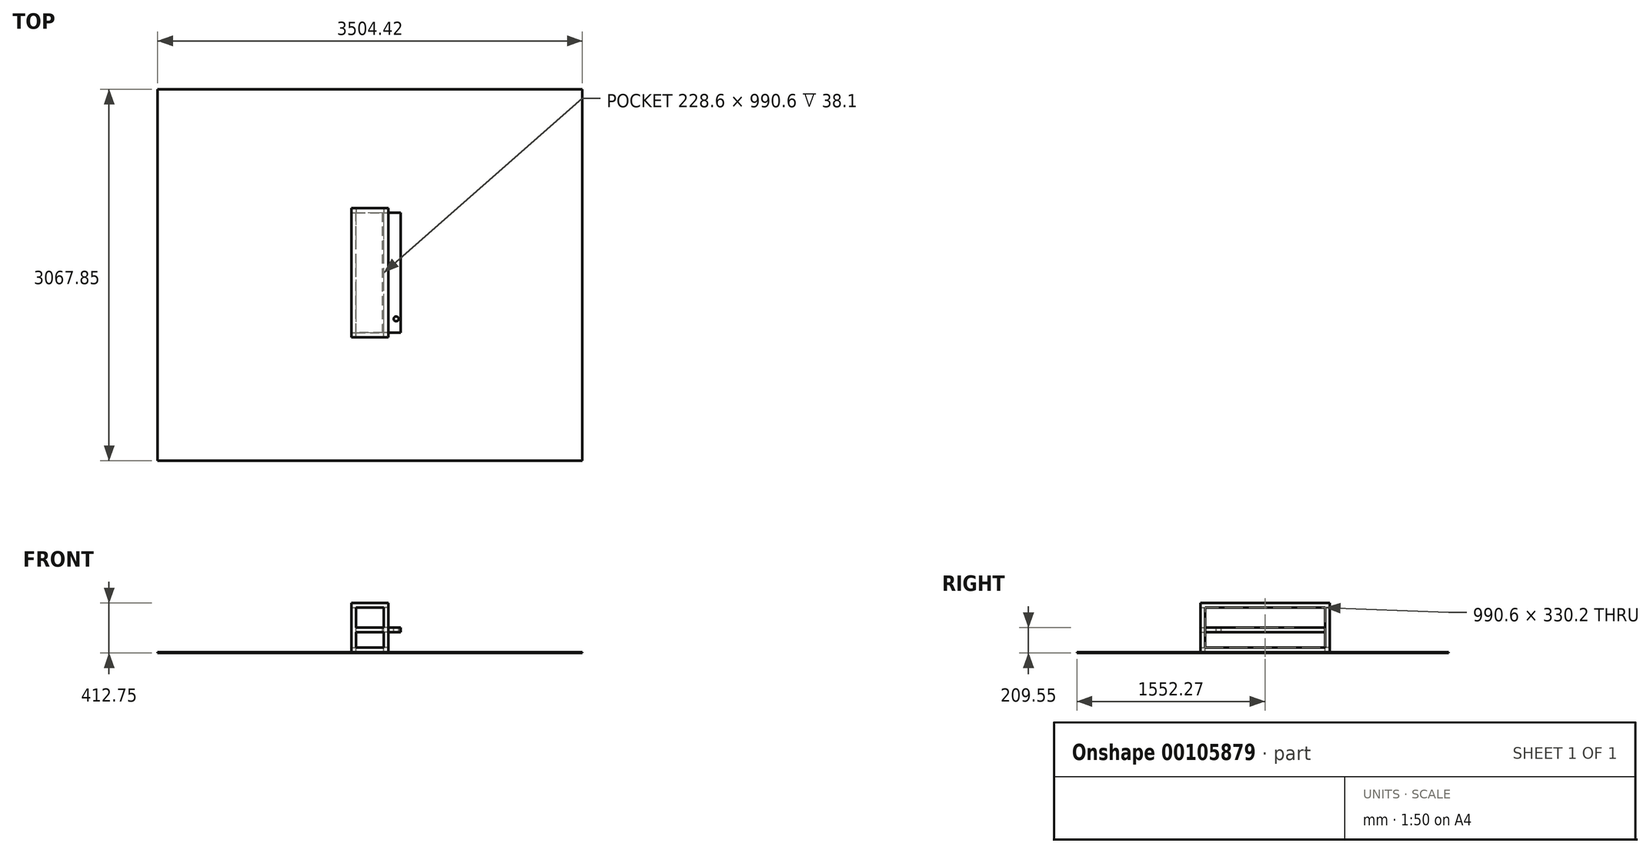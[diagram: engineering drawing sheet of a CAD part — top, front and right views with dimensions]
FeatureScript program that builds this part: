
annotation { "Feature Type Name" : "Feature", "Feature Type Description" : "" }
export const myFeature = defineFeature(function(context is Context, id is Id, definition is map)
    precondition{}
    {
        {
            var Q0;
            Q0=qCreatedBy(makeId("Top.planeOp"),FACE);
            var sketch = newSketch(context, id + "F0", { "sketchPlane" : qUnion([Q0])});
            skLineSegment(sketch, "E0.bottom", {"start": v(-152.4, 0) * mm, "end": v(152.4, 0) * mm});
            skLineSegment(sketch, "E0.top", {"start": v(-152.4, 1066.8) * mm, "end": v(152.4, 1066.8) * mm});
            skLineSegment(sketch, "E0.left", {"start": v(-152.4, 0) * mm, "end": v(-152.4, 1066.8) * mm});
            skLineSegment(sketch, "E0.right", {"start": v(152.4, 0) * mm, "end": v(152.4, 1066.8) * mm});
            skLineSegment(sketch, "E1", {"start": v(-152.4, 533.4) * mm, "end": v(152.4, 533.4) * mm, "construction": true});
            skSolve(sketch);
        }
        {
            var Q0;
            Q0 = qSketchRegion(id + "F0", true);
            extrude(context, id + "F1", {"entities" : qUnion([Q0]), "oppositeDirection" : true, "depth" : 38.1 * mm});
        }
        {
            var Q0;
            Q0=makeQuery(id+"F1.opExtrude","CAP_FACE",FACE,{"disambiguationData":[OSD([sQuery(id+"F0.wireOp",EDGE,"E0.bottom"),sQuery(id+"F0.wireOp",EDGE,"E0.top"),sQuery(id+"F0.wireOp",EDGE,"E0.left"),sQuery(id+"F0.wireOp",EDGE,"E0.right")])],"isStart":false});
            var sketch = newSketch(context, id + "F2", { "sketchPlane" : qUnion([Q0])});
            skLineSegment(sketch, "E2.bottom", {"start": v(-152.4, 0) * mm, "end": v(-114.3, 0) * mm});
            skLineSegment(sketch, "E2.top", {"start": v(-152.4, -38.1) * mm, "end": v(-114.3, -38.1) * mm});
            skLineSegment(sketch, "E2.left", {"start": v(-152.4, 0) * mm, "end": v(-152.4, -38.1) * mm});
            skLineSegment(sketch, "E2.right", {"start": v(-114.3, 0) * mm, "end": v(-114.3, -38.1) * mm});
            skLineSegment(sketch, "E3", {"start": v(0, 0) * mm, "end": v(0, -1066.8) * mm, "construction": true});
            skLineSegment(sketch, "E4", {"start": v(-152.4, -533.4) * mm, "end": v(152.4, -533.4) * mm, "construction": true});
            skLineSegment(sketch, "E5.MirrorCS", {"start": v(152.4, -38.1) * mm, "end": v(114.3, -38.1) * mm});
            skLineSegment(sketch, "E6.MirrorCS", {"start": v(152.4, 0) * mm, "end": v(152.4, -38.1) * mm});
            skLineSegment(sketch, "E7.MirrorCS", {"start": v(152.4, 0) * mm, "end": v(114.3, 0) * mm});
            skLineSegment(sketch, "E8.MirrorCS", {"start": v(114.3, 0) * mm, "end": v(114.3, -38.1) * mm});
            skLineSegment(sketch, "E9.MirrorCS", {"start": v(152.4, -1028.7) * mm, "end": v(114.3, -1028.7) * mm});
            skLineSegment(sketch, "E10.MirrorCS", {"start": v(-152.4, -1028.7) * mm, "end": v(-114.3, -1028.7) * mm});
            skLineSegment(sketch, "E11.MirrorCS", {"start": v(-114.3, -1066.8) * mm, "end": v(-114.3, -1028.7) * mm});
            skLineSegment(sketch, "E12.MirrorCS", {"start": v(114.3, -1066.8) * mm, "end": v(114.3, -1028.7) * mm});
            skLineSegment(sketch, "E13.MirrorCS", {"start": v(-152.4, -1066.8) * mm, "end": v(-114.3, -1066.8) * mm});
            skLineSegment(sketch, "E14.MirrorCS", {"start": v(152.4, -1066.8) * mm, "end": v(114.3, -1066.8) * mm});
            skLineSegment(sketch, "E15.MirrorCS", {"start": v(152.4, -1066.8) * mm, "end": v(152.4, -1028.7) * mm});
            skLineSegment(sketch, "E16.MirrorCS", {"start": v(-152.4, -1066.8) * mm, "end": v(-152.4, -1028.7) * mm});
            skSolve(sketch);
        }
        {
            var Q0;
            Q0 = qSketchRegion(id + "F2", true);
            extrude(context, id + "F3", {"entities" : qUnion([Q0]), "operationType" : NewBodyOperationType.ADD, "depth" : 330.2 * mm});
        }
        {
            var Q0;
            Q0=makeQuery(id+"F3.opExtrude","CAP_FACE",FACE,{"disambiguationData":[OSD([sQuery(id+"F2.wireOp",EDGE,"E2.bottom"),sQuery(id+"F2.wireOp",EDGE,"E2.top"),sQuery(id+"F2.wireOp",EDGE,"E2.left"),sQuery(id+"F2.wireOp",EDGE,"E2.right")])],"isStart":false});
            var sketch = newSketch(context, id + "F4", { "sketchPlane" : qUnion([Q0])});
            skLineSegment(sketch, "E17.bottom", {"start": v(-152.4, 0) * mm, "end": v(152.4, 0) * mm});
            skLineSegment(sketch, "E17.top", {"start": v(-152.4, -1066.8) * mm, "end": v(152.4, -1066.8) * mm});
            skLineSegment(sketch, "E17.left", {"start": v(-152.4, 0) * mm, "end": v(-152.4, -1066.8) * mm});
            skLineSegment(sketch, "E17.right", {"start": v(152.4, 0) * mm, "end": v(152.4, -1066.8) * mm});
            skLineSegment(sketch, "E18.bottom", {"start": v(-114.3, -38.1) * mm, "end": v(114.3, -38.1) * mm});
            skLineSegment(sketch, "E18.top", {"start": v(-114.3, -1028.7) * mm, "end": v(114.3, -1028.7) * mm});
            skLineSegment(sketch, "E18.left", {"start": v(-114.3, -38.1) * mm, "end": v(-114.3, -1028.7) * mm});
            skLineSegment(sketch, "E18.right", {"start": v(114.3, -38.1) * mm, "end": v(114.3, -1028.7) * mm});
            skSolve(sketch);
        }
        {
            var Q0;
            Q0 = qSketchRegion(id + "F4", true);
            extrude(context, id + "F5", {"entities" : qUnion([Q0]), "operationType" : NewBodyOperationType.ADD, "depth" : 38.1 * mm});
        }
        {
            var Q0;
            Q0=makeQuery(id+"F5.boolean.opBoolean","MERGE",FACE,{"derivedFrom":[makeQuery(id+"F3.boolean.opBoolean","MERGE",FACE,{"derivedFrom":[makeQuery(id+"F1.opExtrude","SWEPT_FACE",FACE,{"disambiguationData":[OSD([sQuery(id+"F0.wireOp",EDGE,"E0.bottom")])]}),makeQuery(id+"F3.opExtrude","SWEPT_FACE",FACE,{"disambiguationData":[OSD([sQuery(id+"F2.wireOp",EDGE,"E2.bottom")])]}),makeQuery(id+"F3.opExtrude","SWEPT_FACE",FACE,{"disambiguationData":[OSD([sQuery(id+"F2.wireOp",EDGE,"E7.MirrorCS")])]})]}),makeQuery(id+"F5.opExtrude","SWEPT_FACE",FACE,{"disambiguationData":[OSD([sQuery(id+"F4.wireOp",EDGE,"E17.bottom")])]})]});
            var sketch = newSketch(context, id + "F6", { "sketchPlane" : qUnion([Q0])});
            skCircle(sketch, "E19", {"center": v(152.4, 0) * mm, "radius": 812.8 * mm});
            skLineSegment(sketch, "E20", {"start": v(0, 0) * mm, "end": v(0, 812.8) * mm, "construction": true});
            skCircle(sketch, "E21", {"center": v(783.38, -203.2) * mm, "radius": 812.8 * mm});
            skPoint(sketch, "E22", {"position": v(114.3, -203.2) * mm});
            skSolve(sketch);
        }
        {
            var Q0;
            Q0=makeQuery(id+"F3.opExtrude","SWEPT_FACE",FACE,{"disambiguationData":[OSD([sQuery(id+"F2.wireOp",EDGE,"E2.right")])]});
            var sketch = newSketch(context, id + "F7", { "sketchPlane" : qUnion([Q0])});
            skLineSegment(sketch, "E23.bottom", {"start": v(0, -203.2) * mm, "end": v(38.1, -203.2) * mm});
            skLineSegment(sketch, "E23.top", {"start": v(0, -241.3) * mm, "end": v(38.1, -241.3) * mm});
            skLineSegment(sketch, "E23.left", {"start": v(0, -203.2) * mm, "end": v(0, -241.3) * mm});
            skLineSegment(sketch, "E23.right", {"start": v(38.1, -203.2) * mm, "end": v(38.1, -241.3) * mm});
            skSolve(sketch);
        }
        {
            var Q0;
            Q0 = qSketchRegion(id + "F7", true);
            var Q1;
            Q1=makeQuery(id+"F3.opExtrude","SWEPT_FACE",FACE,{"disambiguationData":[OSD([sQuery(id+"F2.wireOp",EDGE,"E8.MirrorCS")])]});
            extrude(context, id + "F8", {"entities" : qUnion([Q0]), "operationType" : NewBodyOperationType.ADD, "endBound" : BoundingType.UP_TO_SURFACE, "endBoundEntityFace" : qUnion([Q1]), "depth" : 25.4 * mm});
        }
        {
            var Q0;
            Q0=makeQuery(id+"F8.boolean.opBoolean","MERGE",FACE,{"derivedFrom":[makeQuery(id+"F3.opExtrude","SWEPT_FACE",FACE,{"disambiguationData":[OSD([sQuery(id+"F2.wireOp",EDGE,"E2.top")])]}),makeQuery(id+"F3.opExtrude","SWEPT_FACE",FACE,{"disambiguationData":[OSD([sQuery(id+"F2.wireOp",EDGE,"E5.MirrorCS")])]}),makeQuery(id+"F8.opExtrude","SWEPT_FACE",FACE,{"disambiguationData":[OSD([sQuery(id+"F7.wireOp",EDGE,"E23.right")])]})]});
            var sketch = newSketch(context, id + "F9", { "sketchPlane" : qUnion([Q0])});
            skLineSegment(sketch, "E24.bottom", {"start": v(-254, -203.2) * mm, "end": v(-101.6, -203.2) * mm});
            skLineSegment(sketch, "E24.top", {"start": v(-254, -241.3) * mm, "end": v(-101.6, -241.3) * mm});
            skLineSegment(sketch, "E24.left", {"start": v(-254, -203.2) * mm, "end": v(-254, -241.3) * mm});
            skLineSegment(sketch, "E24.right", {"start": v(-101.6, -203.2) * mm, "end": v(-101.6, -241.3) * mm});
            skSolve(sketch);
        }
        {
            var Q0;
            Q0 = qSketchRegion(id + "F9", true);
            var Q1;
            Q1=makeQuery(id+"F3.opExtrude","SWEPT_FACE",FACE,{"disambiguationData":[OSD([sQuery(id+"F2.wireOp",EDGE,"E10.MirrorCS")])]});
            extrude(context, id + "F10", {"entities" : qUnion([Q0]), "operationType" : NewBodyOperationType.ADD, "endBound" : BoundingType.UP_TO_SURFACE, "endBoundEntityFace" : qUnion([Q1]), "depth" : 25.4 * mm});
        }
        {
            var Q0;
            Q0 = qSketchRegion(id + "F9", true);
            var Q1;
            Q1=makeQuery(id+"F3.opExtrude","SWEPT_FACE",FACE,{"disambiguationData":[OSD([sQuery(id+"F2.wireOp",EDGE,"E10.MirrorCS")])]});
            extrude(context, id + "F11", {"entities" : qUnion([Q0]), "operationType" : NewBodyOperationType.ADD, "endBound" : BoundingType.UP_TO_SURFACE, "endBoundEntityFace" : qUnion([Q1]), "depth" : 25.4 * mm});
        }
        {
            var Q0;
            Q0=makeQuery(id+"F10.boolean.opBoolean","MERGE",FACE,{"derivedFrom":[makeQuery(id+"F8.opExtrude","SWEPT_FACE",FACE,{"disambiguationData":[OSD([sQuery(id+"F7.wireOp",EDGE,"E23.bottom")])]}),makeQuery(id+"F10.opExtrude","SWEPT_FACE",FACE,{"disambiguationData":[OSD([sQuery(id+"F9.wireOp",EDGE,"QMmYdaav-W8pb-V5HU-5jat-0M2pRndT3nIR.bottom")])]})]});
            var sketch = newSketch(context, id + "F12", { "sketchPlane" : qUnion([Q0])});
            skCircle(sketch, "E25", {"center": v(215.9, 152.4) * mm, "radius": 20.42 * mm});
            skSolve(sketch);
        }
        {
            var Q0;
            Q0 = qSketchRegion(id + "F12", true);
            extrude(context, id + "F13", {"entities" : qUnion([Q0]), "operationType" : NewBodyOperationType.REMOVE, "endBound" : BoundingType.UP_TO_NEXT, "oppositeDirection" : true, "depth" : 25.4 * mm});
        }
        {
            var Q0;
            Q0=makeQuery(id+"F5.opExtrude","CAP_FACE",FACE,{"disambiguationData":[OSD([sQuery(id+"F4.wireOp",EDGE,"E17.bottom"),sQuery(id+"F4.wireOp",EDGE,"E17.top"),sQuery(id+"F4.wireOp",EDGE,"E17.left"),sQuery(id+"F4.wireOp",EDGE,"E17.right"),sQuery(id+"F4.wireOp",EDGE,"E18.bottom"),sQuery(id+"F4.wireOp",EDGE,"E18.top"),sQuery(id+"F4.wireOp",EDGE,"E18.left"),sQuery(id+"F4.wireOp",EDGE,"E18.right")])],"isStart":false});
            var sketch = newSketch(context, id + "F14", { "sketchPlane" : qUnion([Q0])});
            skLineSegment(sketch, "E26.bottom", {"start": v(1752.2, -2048.98) * mm, "end": v(-1752.2, -2048.98) * mm});
            skLineSegment(sketch, "E26.top", {"start": v(1752.2, 1018.87) * mm, "end": v(-1752.2, 1018.87) * mm});
            skLineSegment(sketch, "E26.left", {"start": v(1752.2, -2048.98) * mm, "end": v(1752.2, 1018.87) * mm});
            skLineSegment(sketch, "E26.right", {"start": v(-1752.2, -2048.98) * mm, "end": v(-1752.2, 1018.87) * mm});
            skPoint(sketch, "E26.middle", {"position": v(0, -515.06) * mm});
            skSolve(sketch);
        }
        {
            var Q0;
            Q0 = qSketchRegion(id + "F14", true);
            extrude(context, id + "F15", {"entities" : qUnion([Q0]), "operationType" : NewBodyOperationType.ADD, "depth" : 6.35 * mm});
        }
    });
